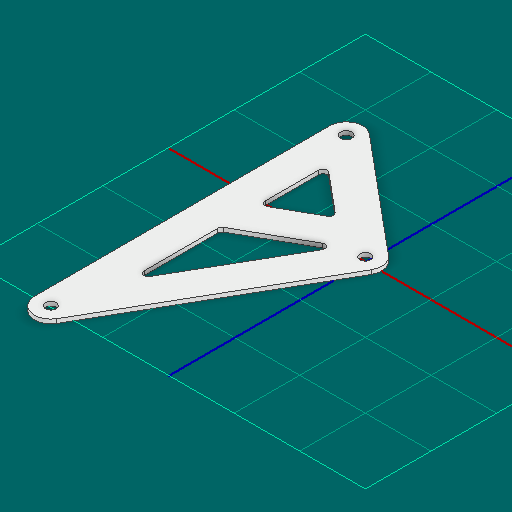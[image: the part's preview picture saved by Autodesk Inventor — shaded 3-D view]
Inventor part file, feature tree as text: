
AUTODESK INVENTOR PART (.ipt)
format: ipt  version: 2025 (Build 290162000, 162)  size: 144,384 bytes
history: native  units: in
note: dims shown in document units (in); Inventor stores cm internally (conversion verified against a paired STEP export)
features: other x3, extrude x1, sketch x1
ambient origin geometry x8: Origin, YZ Plane, XZ Plane, XY Plane, X Axis, Y Axis, Z Axis, Center Point
bodies: Solid1 (feature_tree)
feature tree (5):
  other  "Blocks"
  extrude  "Extrusion1"  Depth=0.0625in TaperAngle=0.0deg
  sketch  "Sketch1"  dims[d1=0.5in d2=0.5in d3=0.5in d4=0.0625in d5=0.5in d6=0.0625in d7=0.0625in d8=0.0625in d9=0.0in d10=4.5in d12=0.5in d13=0.5in d14=0.5192in d16=1.75in d17=0.5in]
  other  "main"
  other  "main:1"
